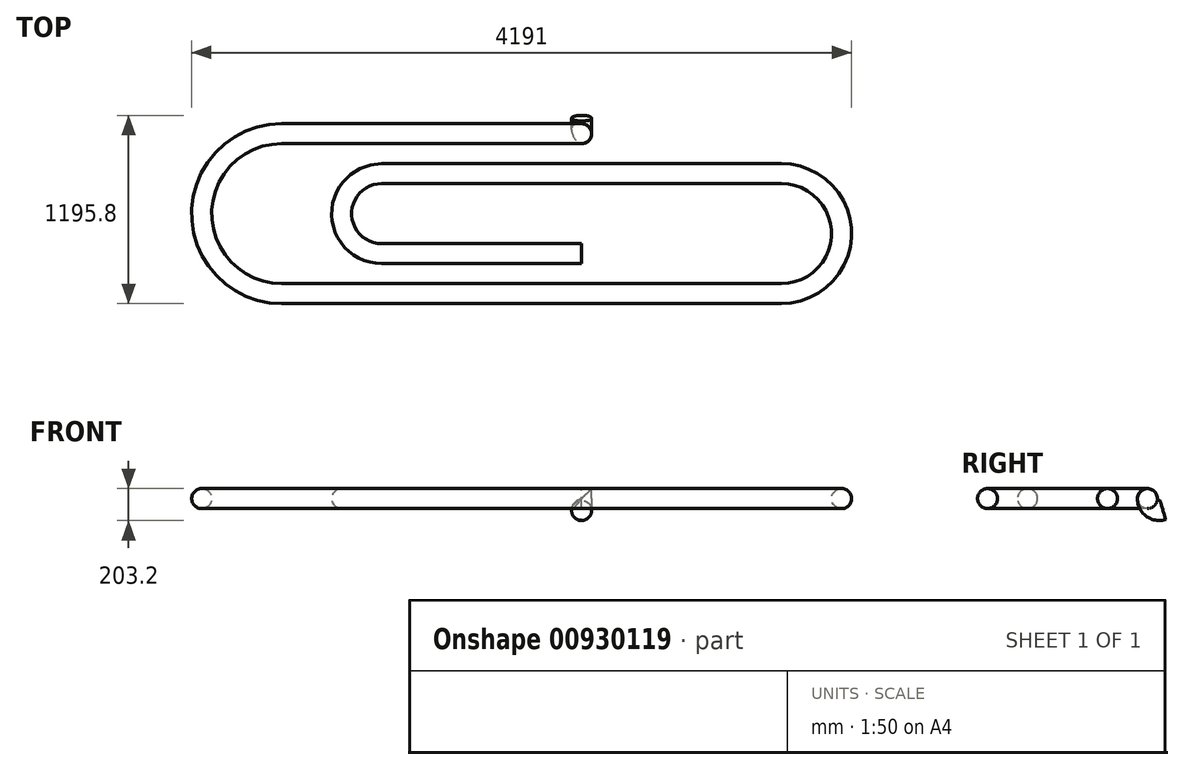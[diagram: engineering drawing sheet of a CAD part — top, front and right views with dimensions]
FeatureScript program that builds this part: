
annotation { "Feature Type Name" : "Feature", "Feature Type Description" : "" }
export const myFeature = defineFeature(function(context is Context, id is Id, definition is map)
    precondition{}
    {
        {
            var Q0;
            Q0=qCreatedBy(makeId("Top.planeOp"),FACE);
            var sketch = newSketch(context, id + "F0", { "sketchPlane" : qUnion([Q0])});
            skLineSegment(sketch, "E0", {"start": v(0, 1154.48) * mm, "end": v(-1905, 1154.48) * mm});
            skLineSegment(sketch, "E1", {"start": v(-1905, 138.48) * mm, "end": v(1270, 138.48) * mm});
            skLineSegment(sketch, "E2", {"start": v(1270, 900.48) * mm, "end": v(-1270, 900.48) * mm});
            skLineSegment(sketch, "E3", {"start": v(-1270, 392.48) * mm, "end": v(0, 392.48) * mm});
            skArc(sketch, "E4", {"start": v(-1905, 1154.48) * mm, "mid": v(-2413, 646.48) * mm, "end": v(-1905, 138.48) * mm});
            skArc(sketch, "E5", {"start": v(-1270, 900.48) * mm, "mid": v(-1524, 646.48) * mm, "end": v(-1270, 392.48) * mm});
            skArc(sketch, "E6", {"start": v(1270, 138.48) * mm, "mid": v(1651, 519.48) * mm, "end": v(1270, 900.48) * mm});
            skSolve(sketch);
        }
        {
            var Q0;
            Q0=qCreatedBy(makeId("Right.planeOp"),FACE);
            var sketch = newSketch(context, id + "F1", { "sketchPlane" : qUnion([Q0])});
            skCircle(sketch, "E7", {"center": v(1154.48, 0) * mm, "radius": 63.5 * mm});
            skArc(sketch, "E8", {"start": v(1154.48, 0) * mm, "mid": v(1185.19, -61.13) * mm, "end": v(1252.55, -73) * mm});
            skSolve(sketch);
        }
        {
            var Q0;
            Q0=makeQuery(id+"F1.imprint","IMPRINT",FACE,{"disambiguationData":[TD([[makeQuery(id+"F1.imprint","IMPRINT",EDGE,{"derivedFrom":sQuery(id+"F1.wireOp",EDGE,"E7")}),1.0]])]});
            var Q1;
            Q1=sQuery(id+"F0.wireOp",EDGE,"E0");
            var Q2;
            Q2=sQuery(id+"F0.wireOp",EDGE,"E4");
            var Q3;
            Q3=sQuery(id+"F0.wireOp",EDGE,"E5");
            var Q4;
            Q4=sQuery(id+"F0.wireOp",EDGE,"E3");
            var Q5;
            Q5=sQuery(id+"F0.wireOp",EDGE,"E2");
            var Q6;
            Q6=sQuery(id+"F0.wireOp",EDGE,"E6");
            var Q7;
            Q7=sQuery(id+"F0.wireOp",EDGE,"E1");
            var Q8;
            Q8=sQuery(id+"F1.wireOp",EDGE,"E8");
            sweep(context, id + "F2", {"profiles" : qUnion([Q0]), "path" : qUnion([Q1, Q2, Q3, Q4, Q5, Q6, Q7, Q8])});
        }
    });
